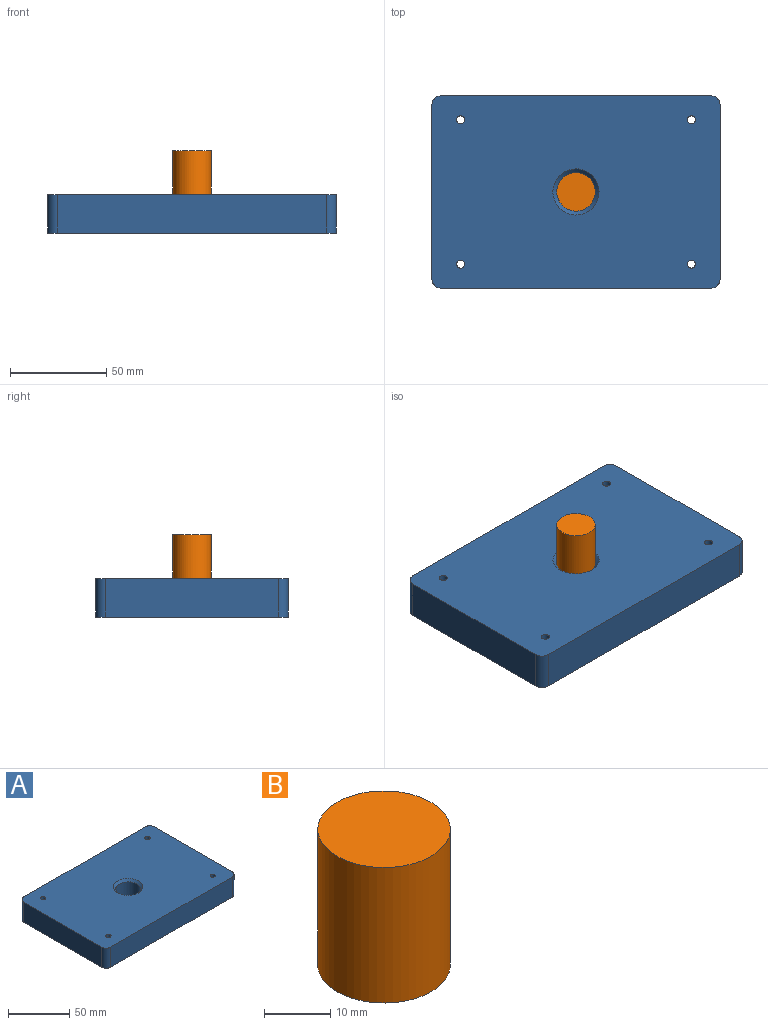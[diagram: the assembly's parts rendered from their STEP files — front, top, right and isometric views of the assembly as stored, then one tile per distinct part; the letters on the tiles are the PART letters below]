
ASSEMBLY  parts=2 mates=1
PART A: 17 faces, bbox 150x100x20 mm
  f0: plane 140x20mm, normal (0,1,0), area 2800mm2, adj f5,f6,f7,f10
  f1: plane 90x20mm, normal (-1,0,0), area 1800mm2, adj f5,f6,f7,f8
  f2: plane 140x20mm, normal (0,-1,0), area 2800mm2, adj f5,f6,f8,f9
  f3: cylinder r=10mm len=20mm, axis (0,0,-1), area 1005.3mm2, adj f11,f12
  f4: plane 90x20mm, normal (1,0,0), area 1800mm2, adj f5,f6,f9,f10
  f5: plane 150x100mm, normal (0,0,1), area 14470.7mm2, adj f0,f1,f2,f4,f7,f8,f9,f10
  f6: plane 150x100mm, normal (0,0,-1), area 14470.7mm2, adj f0,f1,f2,f4,f7,f8,f9,f10
  f7: cylinder r=5mm len=20mm, axis (0,0,1), area 157.1mm2, adj f0,f1,f5,f6
  f8: cylinder r=5mm len=20mm, axis (0,0,-1), area 157.1mm2, adj f1,f2,f5,f6
  f9: cylinder r=5mm len=20mm, axis (0,0,1), area 157.1mm2, adj f2,f4,f5,f6
  f10: cylinder r=5mm len=20mm, axis (0,0,-1), area 157.1mm2, adj f0,f4,f5,f6
  f11: cone r=10mm half-angle=45deg, axis (0,0,1), area 195.5mm2, adj f3,f5
  f12: cone r=12mm half-angle=45deg, axis (0,0,-1), area 195.5mm2, adj f3,f6
  f13: cylinder r=2.1mm len=20mm, axis (0,0,-1), area 263.9mm2, adj f5,f6
  f14: cylinder r=2.1mm len=20mm, axis (0,0,-1), area 263.9mm2, adj f5,f6
  f15: cylinder r=2.1mm len=20mm, axis (0,0,-1), area 263.9mm2, adj f5,f6
  f16: cylinder r=2.1mm len=20mm, axis (0,0,-1), area 263.9mm2, adj f5,f6
PART B: 3 faces, bbox 20x20x25 mm
  f0: cylinder r=10mm len=25mm, axis (0,0,-1), area 1570.8mm2, adj f1,f2
  f1: plane 20x20mm, normal (0,0,1), area 314.2mm2, adj f0
  f2: plane 20x20mm, normal (0,0,-1), area 314.2mm2, adj f0
PLACE A rot(axis=(0,0,-1),0deg) t=(0,0,-10)mm fixed
PLACE B rot(axis=(1,0,0),0deg) t=(0,0,7.7)mm
MATE slider A.f3 <-> B.f0  axis (0,0,1) through (0,0,10)mm
